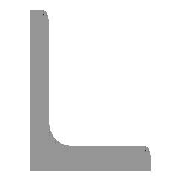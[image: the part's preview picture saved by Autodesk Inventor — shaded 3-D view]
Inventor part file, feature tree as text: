
AUTODESK INVENTOR PART (.ipt)
format: ipt  version: 2013 (Build 170138000, 138)  size: 130,048 bytes
history: native  units: mm (DEFAULTED — no unit token found)
features: other x4, plane x3, split x2, sketch x2
ambient origin geometry x8: Origin, YZ Plane, XZ Plane, XY Plane, X Axis, Y Axis, Z Axis, Center Point
bodies: Solid1 (feature_tree), Body (feature_tree)
feature tree (11):
  parser-record x1  (decoder bookkeeping rows leaked as tree rows — omitted from the tree; the rows remain in map.json)
  other  "Driven Length"
  other  "Start plane"
  other  "End plane"
  plane  "Work Plane4"
  split  "Split1"
  plane  "Work Plane5"
  split  "Split2"
  sketch  "Sketch3"  dims[d0=38.1mm]
  plane  "Work Plane3"
  sketch  "Sketch4"  dims[d1=38.1mm d2=4.7625mm d3=4.7625mm d4=558.8mm d5=0.0mm d10=0.0mm d11=0.0mm d12=-0.0mm d13=558.8mm d14=4.826mm d15=2.286mm d16=90.0deg d17=558.8mm]
